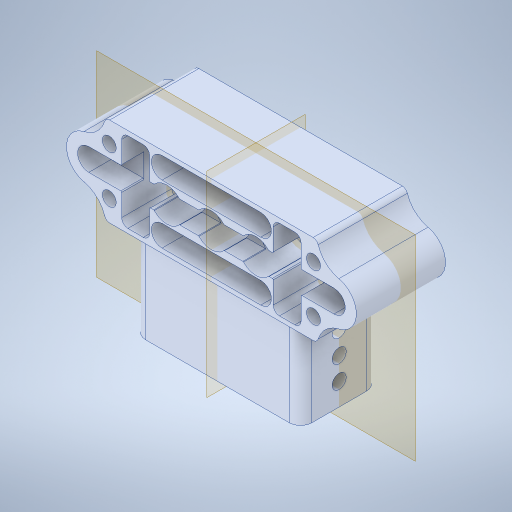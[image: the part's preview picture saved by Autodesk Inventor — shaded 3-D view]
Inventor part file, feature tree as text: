
AUTODESK INVENTOR PART (.ipt)
format: ipt  version: 2023.4 (Build 274418000, 418)  size: 478,208 bytes
history: native  units: in
note: dims shown in document units (in); Inventor stores cm internally (conversion verified against a paired STEP export)
features: fillet x1
ambient origin geometry x8: Origin, YZ Plane, XZ Plane, XY Plane, X Axis, Y Axis, Z Axis, Center Point
bodies: Solid1 (feature_tree)
feature tree (1):
  fillet  "Fillet6"  [1 undecoded]
note: 1 required parameter value undecoded (feature->parameter linkage not recoverable at this tier; creation-order binding heuristic only, values carry confidence <= 0.55)
